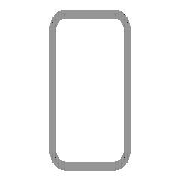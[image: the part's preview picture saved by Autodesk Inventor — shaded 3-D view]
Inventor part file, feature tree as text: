
AUTODESK INVENTOR PART (.ipt)
format: ipt  version: 2025 (Build 290162010, 162A)  size: 148,992 bytes
history: native  units: mm (DEFAULTED — no unit token found)
features: other x4, plane x3, split x2, sketch x1
ambient origin geometry x8: Origin, YZ Plane, XZ Plane, XY Plane, X Axis, Y Axis, Z Axis, Center Point
bodies: Solid1 (feature_tree), Body (feature_tree)
feature tree (10):
  parser-record x1  (decoder bookkeeping rows leaked as tree rows — omitted from the tree; the rows remain in map.json)
  other  "Driven Length"
  other  "Start Plane"
  other  "End Plane"
  plane  "Work Plane4"
  split  "Split1"
  plane  "Work Plane5"
  split  "Split2"
  sketch  "Sketch3"  dims[d3=637.837057mm d4=0.0mm d7=8.0mm d9=50.0mm d11=100.0mm d12=4.0mm d13=65.085414mm d14=702.922471mm d15=25.0mm d16=50.0mm d17=90.0deg d18=637.837057mm]
  plane  "Work Plane3"
